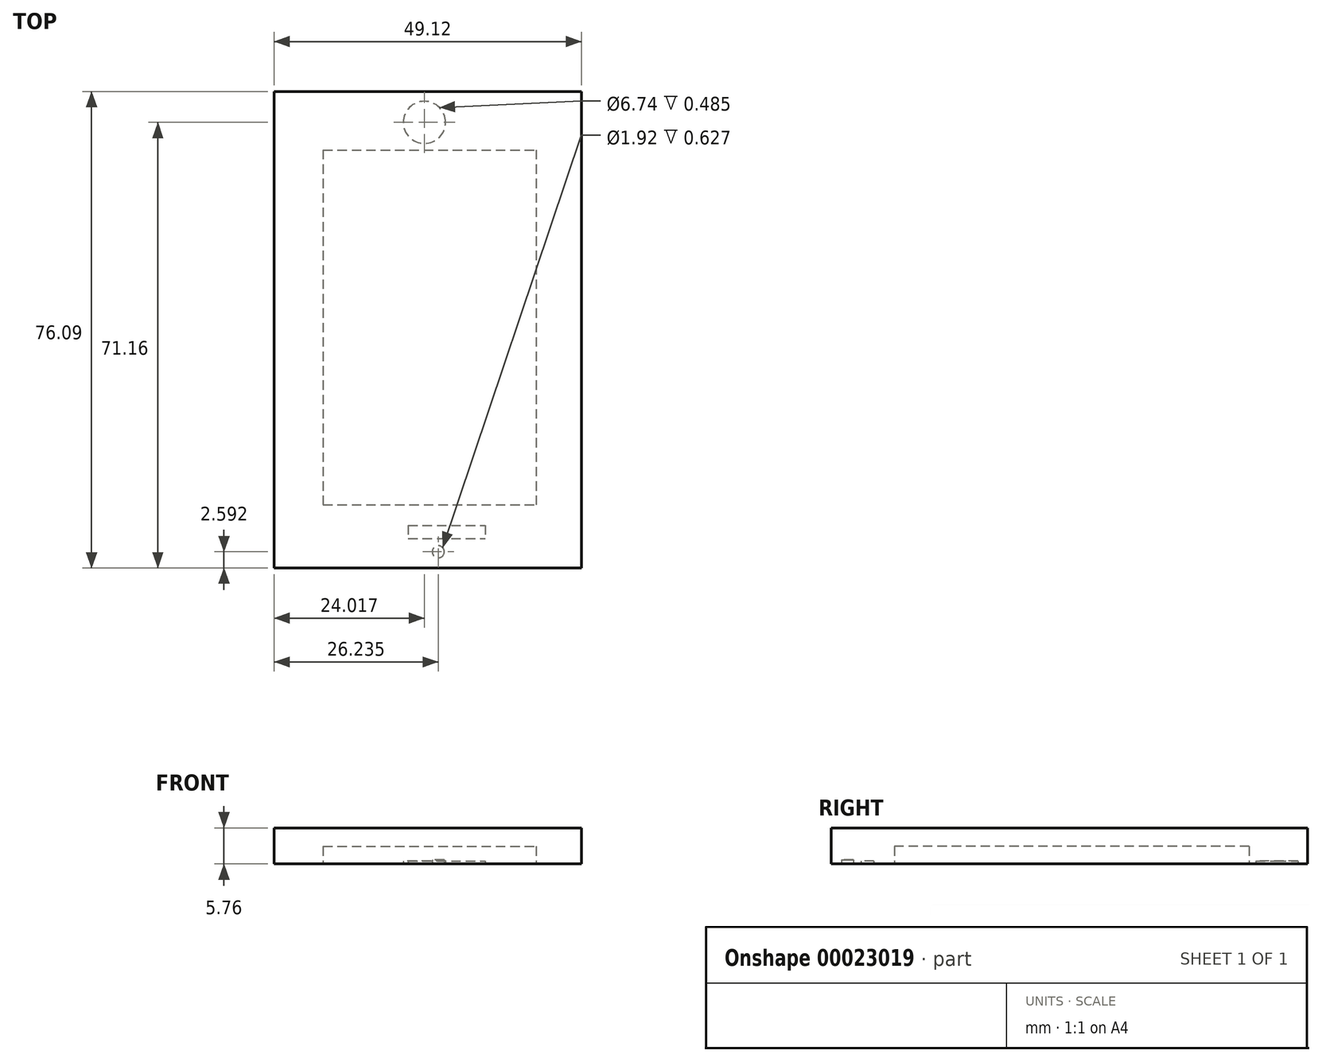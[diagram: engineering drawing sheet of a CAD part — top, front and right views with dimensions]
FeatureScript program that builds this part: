
annotation { "Feature Type Name" : "Feature", "Feature Type Description" : "" }
export const myFeature = defineFeature(function(context is Context, id is Id, definition is map)
    precondition{}
    {
        {
            var Q0;
            Q0=qCreatedBy(makeId("Top.planeOp"),FACE);
            var sketch = newSketch(context, id + "F0", { "sketchPlane" : qUnion([Q0])});
            skLineSegment(sketch, "E0.bottom", {"start": v(0, 0) * mm, "end": v(49.12, 0) * mm});
            skLineSegment(sketch, "E0.top", {"start": v(0, 76.1) * mm, "end": v(49.12, 76.1) * mm});
            skLineSegment(sketch, "E0.left", {"start": v(0, 0) * mm, "end": v(0, 76.1) * mm});
            skLineSegment(sketch, "E0.right", {"start": v(49.12, 0) * mm, "end": v(49.12, 76.1) * mm});
            skSolve(sketch);
        }
        {
            var Q0;
            Q0=makeQuery(id+"F0.imprint","IMPRINT",FACE,{"disambiguationData":[TD([[makeQuery(id+"F0.imprint","IMPRINT",EDGE,{"derivedFrom":sQuery(id+"F0.wireOp",EDGE,"E0.bottom")}),1.0]])]});
            extrude(context, id + "F1", {"entities" : qUnion([Q0]), "depth" : 5.76 * mm});
        }
        {
            var Q0;
            Q0=qCreatedBy(makeId("Top.planeOp"),FACE);
            var sketch = newSketch(context, id + "F2", { "sketchPlane" : qUnion([Q0])});
            skLineSegment(sketch, "E1.bottom", {"start": v(7.84, 66.75) * mm, "end": v(41.89, 66.75) * mm});
            skLineSegment(sketch, "E1.top", {"start": v(7.84, 10.1) * mm, "end": v(41.89, 10.1) * mm});
            skLineSegment(sketch, "E1.left", {"start": v(7.84, 66.75) * mm, "end": v(7.84, 10.1) * mm});
            skLineSegment(sketch, "E1.right", {"start": v(41.89, 66.75) * mm, "end": v(41.89, 10.1) * mm});
            skSolve(sketch);
        }
        {
            var Q0;
            Q0=makeQuery(id+"F2.imprint","IMPRINT",FACE,{"disambiguationData":[TD([[makeQuery(id+"F2.imprint","IMPRINT",EDGE,{"derivedFrom":sQuery(id+"F2.wireOp",EDGE,"E1.bottom")}),-1.0]])]});
            extrude(context, id + "F3", {"entities" : qUnion([Q0]), "operationType" : NewBodyOperationType.REMOVE, "depth" : 2.8 * mm});
        }
        {
            var Q0;
            Q0=qCreatedBy(makeId("Top.planeOp"),FACE);
            var sketch = newSketch(context, id + "F4", { "sketchPlane" : qUnion([Q0])});
            skCircle(sketch, "E2", {"center": v(24.02, 71.16) * mm, "radius": 3.37 * mm});
            skSolve(sketch);
        }
        {
            var Q0;
            Q0=makeQuery(id+"F4.imprint","IMPRINT",FACE,{"disambiguationData":[TD([[makeQuery(id+"F4.imprint","IMPRINT",EDGE,{"derivedFrom":sQuery(id+"F4.wireOp",EDGE,"E2")}),1.0]])]});
            var Q1;
            Q1=sQuery(id+"F4.wireOp",EDGE,"E2");
            extrude(context, id + "F5", {"entities" : qUnion([Q0]), "operationType" : NewBodyOperationType.REMOVE, "surfaceEntities" : qUnion([Q1]), "depth" : 0.48 * mm});
        }
        {
            var Q0;
            Q0=qCreatedBy(makeId("Top.planeOp"),FACE);
            var sketch = newSketch(context, id + "F6", { "sketchPlane" : qUnion([Q0])});
            skLineSegment(sketch, "E3.bottom", {"start": v(21.42, 6.83) * mm, "end": v(33.73, 6.83) * mm});
            skLineSegment(sketch, "E3.top", {"start": v(21.42, 4.74) * mm, "end": v(33.73, 4.74) * mm});
            skLineSegment(sketch, "E3.left", {"start": v(21.42, 6.83) * mm, "end": v(21.42, 4.74) * mm});
            skLineSegment(sketch, "E3.right", {"start": v(33.73, 6.83) * mm, "end": v(33.73, 4.74) * mm});
            skSolve(sketch);
        }
        {
            var Q0;
            Q0=makeQuery(id+"F6.imprint","IMPRINT",FACE,{"disambiguationData":[TD([[makeQuery(id+"F6.imprint","IMPRINT",EDGE,{"derivedFrom":sQuery(id+"F6.wireOp",EDGE,"E3.bottom")}),-1.0]])]});
            extrude(context, id + "F7", {"entities" : qUnion([Q0]), "operationType" : NewBodyOperationType.REMOVE, "depth" : 0.44 * mm});
        }
        {
            var Q0;
            Q0=makeQuery(id+"F1.opExtrude","SWEPT_FACE",FACE,{"disambiguationData":[OSD([sQuery(id+"F0.wireOp",EDGE,"E0.right")])]});
            var sketch = newSketch(context, id + "F8", { "sketchPlane" : qUnion([Q0])});
            skCircle(sketch, "E4", {"center": v(16.67, 5.73) * mm, "radius": 1.57 * mm});
            skSolve(sketch);
        }
        {
            var Q0;
            Q0=makeQuery(id+"F8.imprint","IMPRINT",FACE,{"disambiguationData":[TD([[makeQuery(id+"F8.imprint","IMPRINT",EDGE,{"derivedFrom":sQuery(id+"F8.wireOp",EDGE,"E4")}),1.0]])]});
            extrude(context, id + "F9", {"entities" : qUnion([Q0]), "operationType" : NewBodyOperationType.REMOVE, "depth" : 0.74 * mm});
        }
        {
            var Q0;
            Q0=qCreatedBy(makeId("Top.planeOp"),FACE);
            var sketch = newSketch(context, id + "F10", { "sketchPlane" : qUnion([Q0])});
            skCircle(sketch, "E5", {"center": v(26.23, 2.6) * mm, "radius": 0.96 * mm});
            skSolve(sketch);
        }
        {
            var Q0;
            Q0=makeQuery(id+"F10.imprint","IMPRINT",FACE,{"disambiguationData":[TD([[makeQuery(id+"F10.imprint","IMPRINT",EDGE,{"derivedFrom":sQuery(id+"F10.wireOp",EDGE,"E5")}),1.0]])]});
            extrude(context, id + "F11", {"entities" : qUnion([Q0]), "operationType" : NewBodyOperationType.REMOVE, "depth" : 0.63 * mm});
        }
    });
